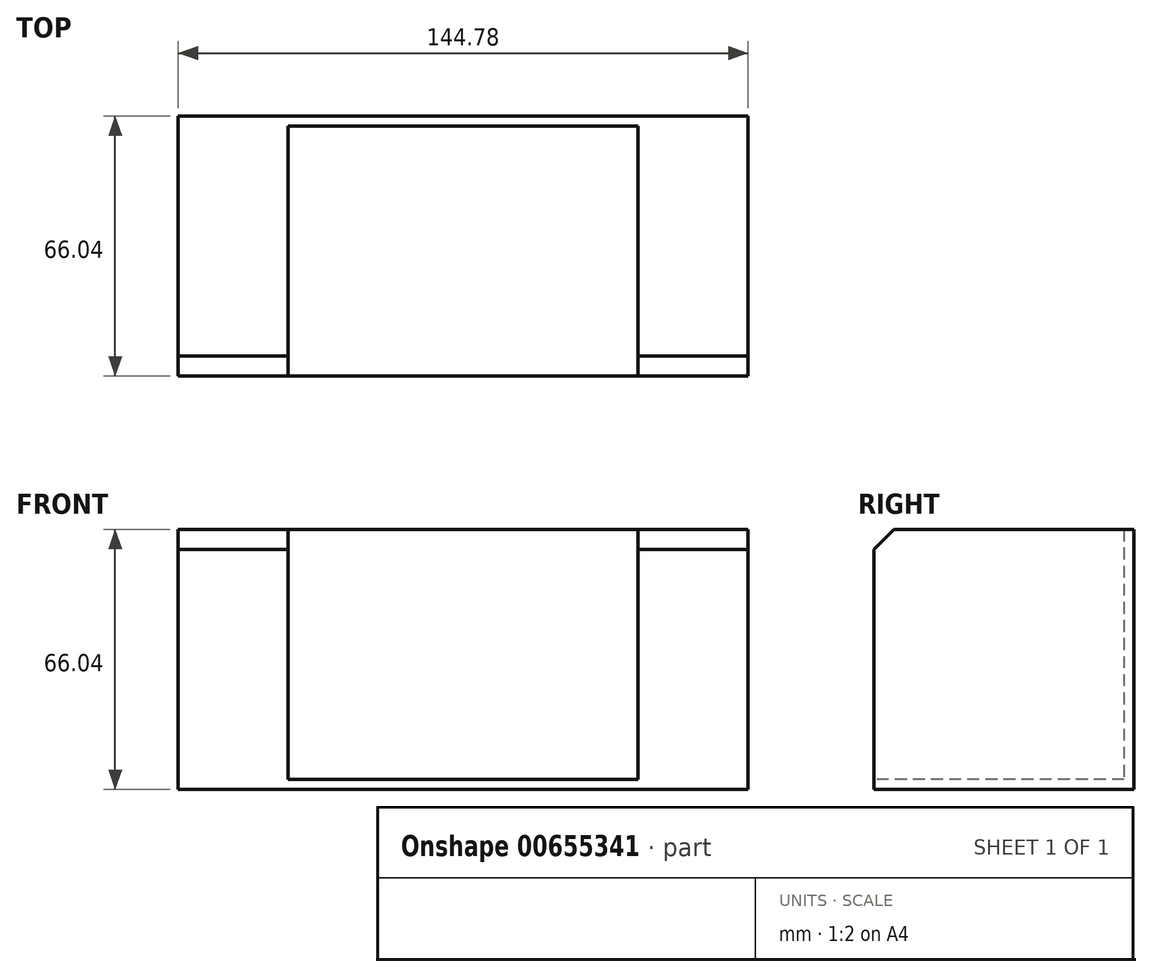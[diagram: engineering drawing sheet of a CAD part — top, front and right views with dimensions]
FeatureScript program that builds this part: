
annotation { "Feature Type Name" : "Feature", "Feature Type Description" : "" }
export const myFeature = defineFeature(function(context is Context, id is Id, definition is map)
    precondition{}
    {
        {
            var Q0;
            Q0=qCreatedBy(makeId("Top.planeOp"),FACE);
            var sketch = newSketch(context, id + "F0", { "sketchPlane" : qUnion([Q0])});
            skLineSegment(sketch, "E0.bottom", {"start": v(-48.43, 7.43) * mm, "end": v(65.87, 7.43) * mm});
            skLineSegment(sketch, "E0.top", {"start": v(-48.43, -56.07) * mm, "end": v(65.87, -56.07) * mm});
            skLineSegment(sketch, "E0.left", {"start": v(-48.43, 7.43) * mm, "end": v(-48.43, -56.07) * mm});
            skLineSegment(sketch, "E0.right", {"start": v(65.87, 7.43) * mm, "end": v(65.87, -56.07) * mm});
            skSolve(sketch);
        }
        {
            var Q0;
            Q0 = qSketchRegion(id + "F0", true);
            extrude(context, id + "F1", {"entities" : qUnion([Q0]), "depth" : 63.5 * mm, "offsetDistance" : 25.4 * mm});
        }
        {
            var Q0;
            Q0=makeQuery(id+"F1.opExtrude","CAP_EDGE",EDGE,{"disambiguationData":[OSD([sQuery(id+"F0.wireOp",EDGE,"E0.top")])],"isStart":false});
            chamfer(context, id + "F2", {"entities" : qUnion([Q0]), "width" : 5.08 * mm, "tangentPropagation" : true});
        }
        {
            var Q0;
            Q0=makeQuery(id+"F1.opExtrude","CAP_FACE",FACE,{"disambiguationData":[OSD([sQuery(id+"F0.wireOp",EDGE,"E0.bottom"),sQuery(id+"F0.wireOp",EDGE,"E0.top"),sQuery(id+"F0.wireOp",EDGE,"E0.left"),sQuery(id+"F0.wireOp",EDGE,"E0.right")])],"isStart":false});
            var Q1;
            Q1=makeQuery(id+"F1.opExtrude","SWEPT_FACE",FACE,{"disambiguationData":[OSD([sQuery(id+"F0.wireOp",EDGE,"E0.top")])]});
            var Q2;
            Q2=makeQuery(id+"F2.opChamfer","BLEND_FACE",FACE,{"disambiguationData":[OSD([sQuery(id+"F0.wireOp",EDGE,"E0.top")])]});
            shell(context, id + "F3", {"entities" : qUnion([Q0, Q1, Q2]), "thickness" : 2.54 * mm, "oppositeDirection" : true});
        }
        {
            var Q0;
            Q0=makeQuery(id+"F1.opExtrude","SWEPT_FACE",FACE,{"disambiguationData":[OSD([sQuery(id+"F0.wireOp",EDGE,"E0.right")])]});
            var Q1;
            Q1=makeQuery(id+"F3.opShell","OFFSET_FACE",FACE,{"disambiguationData":[OSD([sQuery(id+"F0.wireOp",EDGE,"E0.left")])]});
            extrude(context, id + "F4", {"entities" : qUnion([Q0, Q1]), "operationType" : NewBodyOperationType.ADD, "depth" : 25.4 * mm, "offsetDistance" : 25.4 * mm});
        }
    });
